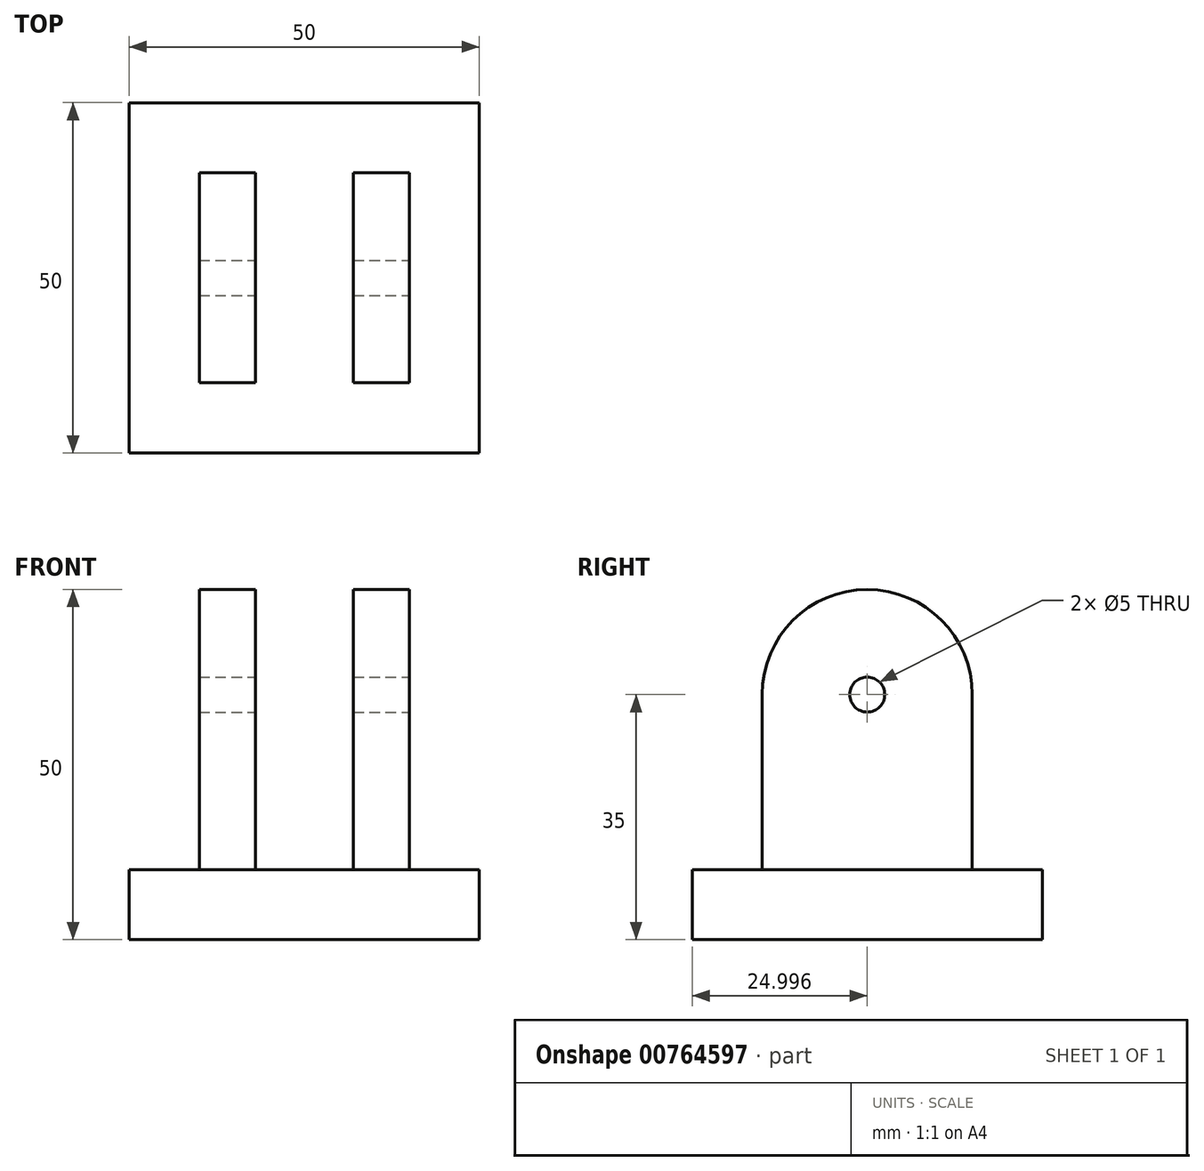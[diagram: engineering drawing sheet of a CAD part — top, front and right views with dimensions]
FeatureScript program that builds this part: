
annotation { "Feature Type Name" : "Feature", "Feature Type Description" : "" }
export const myFeature = defineFeature(function(context is Context, id is Id, definition is map)
    precondition{}
    {
        {
            var Q0;
            Q0=qCreatedBy(makeId("Top.planeOp"),FACE);
            var sketch = newSketch(context, id + "F0", { "sketchPlane" : qUnion([Q0])});
            skLineSegment(sketch, "E0.bottom", {"start": v(-23.98, 25.18) * mm, "end": v(26.02, 25.18) * mm});
            skLineSegment(sketch, "E0.top", {"start": v(-23.98, -24.82) * mm, "end": v(26.02, -24.82) * mm});
            skLineSegment(sketch, "E0.left", {"start": v(-23.98, 25.18) * mm, "end": v(-23.98, -24.82) * mm});
            skLineSegment(sketch, "E0.right", {"start": v(26.02, 25.18) * mm, "end": v(26.02, -24.82) * mm});
            skSolve(sketch);
        }
        {
            var Q0;
            Q0=makeQuery(id+"F0.imprint","IMPRINT",FACE,{"disambiguationData":[TD([[makeQuery(id+"F0.imprint","IMPRINT",EDGE,{"derivedFrom":sQuery(id+"F0.wireOp",EDGE,"E0.bottom")}),-1.0]])]});
            extrude(context, id + "F1", {"entities" : qUnion([Q0]), "depth" : 10 * mm, "offsetDistance" : 25 * mm});
        }
        {
            var Q0;
            Q0=makeQuery(id+"F1.opExtrude","CAP_FACE",FACE,{"disambiguationData":[OSD([sQuery(id+"F0.wireOp",EDGE,"E0.bottom"),sQuery(id+"F0.wireOp",EDGE,"E0.top"),sQuery(id+"F0.wireOp",EDGE,"E0.left"),sQuery(id+"F0.wireOp",EDGE,"E0.right")])],"isStart":false});
            var sketch = newSketch(context, id + "F2", { "sketchPlane" : qUnion([Q0])});
            skLineSegment(sketch, "E1.bottom", {"start": v(-13.98, 15.18) * mm, "end": v(-5.98, 15.18) * mm});
            skLineSegment(sketch, "E1.top", {"start": v(-13.98, -14.82) * mm, "end": v(-5.98, -14.82) * mm});
            skLineSegment(sketch, "E1.left", {"start": v(-13.98, 15.18) * mm, "end": v(-13.98, -14.82) * mm});
            skLineSegment(sketch, "E1.right", {"start": v(-5.98, 15.18) * mm, "end": v(-5.98, -14.82) * mm});
            skLineSegment(sketch, "E2.bottom", {"start": v(8.02, 15.18) * mm, "end": v(16.02, 15.18) * mm});
            skLineSegment(sketch, "E2.top", {"start": v(8.02, -14.82) * mm, "end": v(16.02, -14.82) * mm});
            skLineSegment(sketch, "E2.left", {"start": v(8.02, 15.18) * mm, "end": v(8.02, -14.82) * mm});
            skLineSegment(sketch, "E2.right", {"start": v(16.02, 15.18) * mm, "end": v(16.02, -14.82) * mm});
            skSolve(sketch);
        }
        {
            var Q0;
            Q0=makeQuery(id+"F2.imprint","IMPRINT",FACE,{"disambiguationData":[TD([[makeQuery(id+"F2.imprint","IMPRINT",EDGE,{"derivedFrom":sQuery(id+"F2.wireOp",EDGE,"E1.bottom")}),-1.0]])]});
            var Q1;
            Q1=makeQuery(id+"F2.imprint","IMPRINT",FACE,{"disambiguationData":[TD([[makeQuery(id+"F2.imprint","IMPRINT",EDGE,{"derivedFrom":sQuery(id+"F2.wireOp",EDGE,"E2.bottom")}),-1.0]])]});
            extrude(context, id + "F3", {"entities" : qUnion([Q0, Q1]), "operationType" : NewBodyOperationType.ADD, "depth" : 40 * mm, "offsetDistance" : 25 * mm});
        }
        {
            var Q0;
            Q0=makeQuery(id+"F3.opExtrude","CAP_EDGE",EDGE,{"disambiguationData":[OSD([sQuery(id+"F2.wireOp",EDGE,"E2.top")])],"isStart":false});
            var Q1;
            Q1=makeQuery(id+"F3.opExtrude","CAP_EDGE",EDGE,{"disambiguationData":[OSD([sQuery(id+"F2.wireOp",EDGE,"E2.bottom")])],"isStart":false});
            var Q2;
            Q2=makeQuery(id+"F3.opExtrude","CAP_EDGE",EDGE,{"disambiguationData":[OSD([sQuery(id+"F2.wireOp",EDGE,"E1.top")])],"isStart":false});
            var Q3;
            Q3=makeQuery(id+"F3.opExtrude","CAP_EDGE",EDGE,{"disambiguationData":[OSD([sQuery(id+"F2.wireOp",EDGE,"E1.bottom")])],"isStart":false});
            fillet(context, id + "F4", {"entities" : qUnion([Q0, Q1, Q2, Q3]), "radius" : 15 * mm, "tangentPropagation" : true, "allowEdgeOverflow" : false});
        }
        {
            var Q0;
            Q0=makeQuery(id+"F3.opExtrude","SWEPT_FACE",FACE,{"disambiguationData":[OSD([sQuery(id+"F2.wireOp",EDGE,"E2.right")])]});
            var sketch = newSketch(context, id + "F5", { "sketchPlane" : qUnion([Q0])});
            skPoint(sketch, "E3", {"position": v(0.18, 35) * mm});
            skSolve(sketch);
        }
        {
            var Q0;
            Q0=sQuery(id+"F5.wireOp",VERTEX,"E3");
            var Q1;
            Q1=makeQuery(id+"F1.opExtrude","SWEPT_BODY",BODY,{"disambiguationData":[OSD([sQuery(id+"F0.wireOp",EDGE,"E0.bottom"),sQuery(id+"F0.wireOp",EDGE,"E0.top"),sQuery(id+"F0.wireOp",EDGE,"E0.left"),sQuery(id+"F0.wireOp",EDGE,"E0.right")])]});
            hole(context, id + "F6", {"style" : HoleStyle.SIMPLE, "endStyle" : HoleEndStyle.THROUGH, "holeDiameter" : 5 * mm, "majorDiameter" : 5 * mm, "isTappedThrough" : true, "tappedDepth" : 12 * mm, "tapClearance" : 3, "locations" : qUnion([Q0]), "scope" : qUnion([Q1])});
        }
    });
